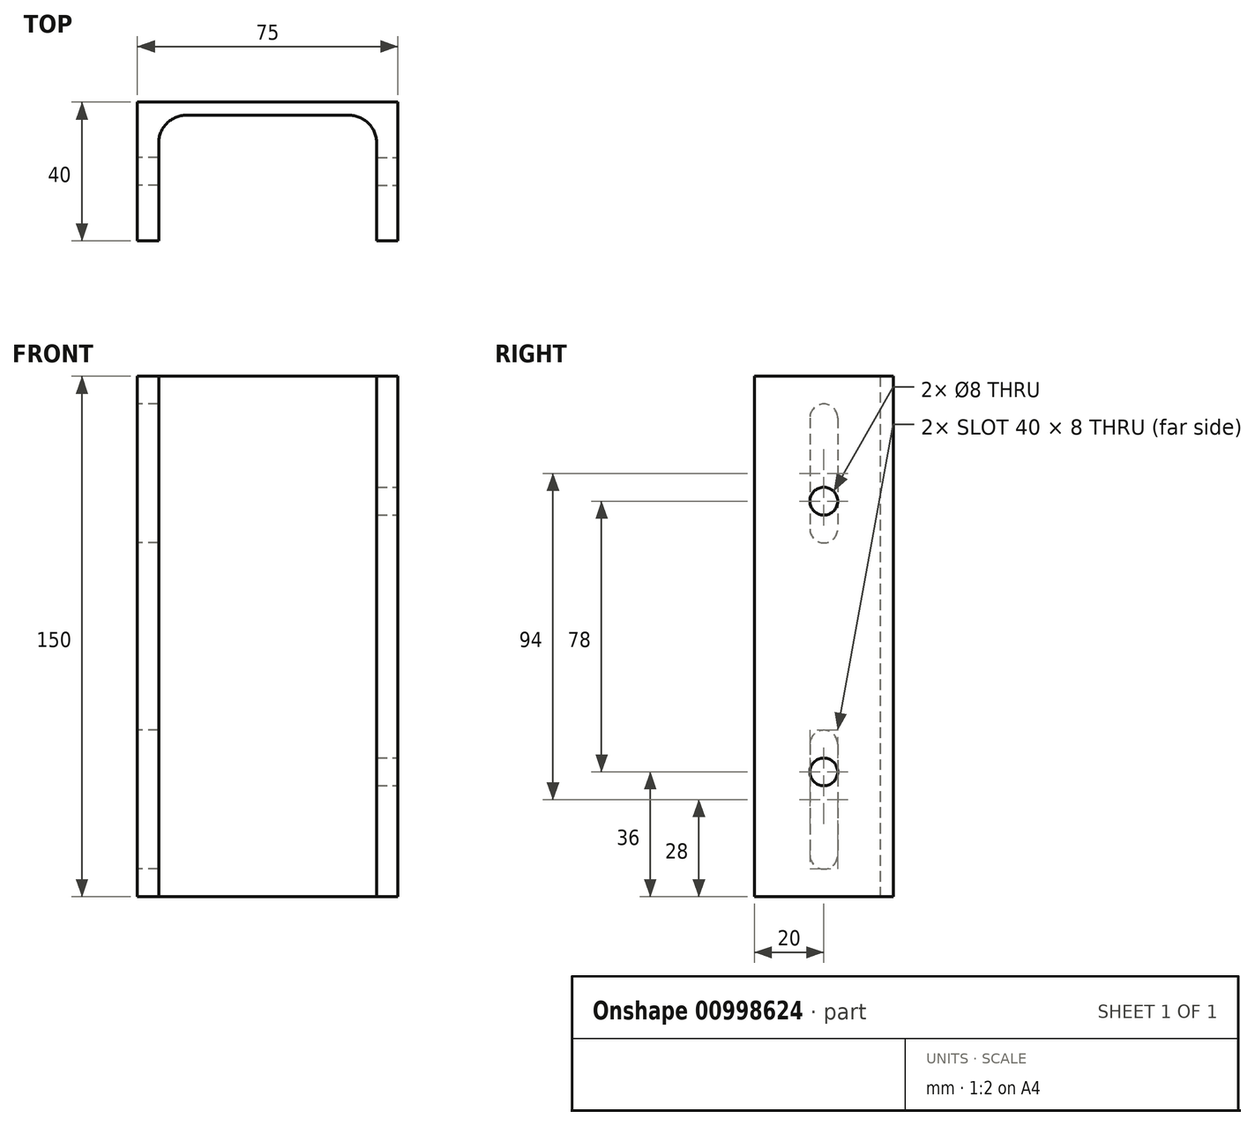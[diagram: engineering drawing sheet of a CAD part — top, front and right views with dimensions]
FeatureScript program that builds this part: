
annotation { "Feature Type Name" : "Feature", "Feature Type Description" : "" }
export const myFeature = defineFeature(function(context is Context, id is Id, definition is map)
    precondition{}
    {
        {
            var Q0;
            Q0=qCreatedBy(makeId("Top.planeOp"),FACE);
            var sketch = newSketch(context, id + "F0", { "sketchPlane" : qUnion([Q0])});
            skLineSegment(sketch, "E0", {"start": v(-37.5, 0) * mm, "end": v(37.5, 0) * mm});
            skLineSegment(sketch, "E1", {"start": v(-37.5, 0) * mm, "end": v(-37.5, -40) * mm});
            skLineSegment(sketch, "E2", {"start": v(37.5, 0) * mm, "end": v(37.5, -40) * mm});
            skLineSegment(sketch, "E3", {"start": v(-31.4, -11.8) * mm, "end": v(-31.4, -40) * mm});
            skLineSegment(sketch, "E4", {"start": v(-31.4, -40) * mm, "end": v(-37.5, -40) * mm});
            skLineSegment(sketch, "E5", {"start": v(31.4, -11.8) * mm, "end": v(31.4, -40) * mm});
            skLineSegment(sketch, "E6", {"start": v(31.4, -40) * mm, "end": v(37.5, -40) * mm});
            skArc(sketch, "E7", {"start": v(-23.4, -3.8) * mm, "mid": v(-29.06, -6.14) * mm, "end": v(-31.4, -11.8) * mm});
            skArc(sketch, "E8", {"start": v(31.4, -11.8) * mm, "mid": v(29.06, -6.14) * mm, "end": v(23.4, -3.8) * mm});
            skLineSegment(sketch, "E9.trimOffspring", {"start": v(-23.4, -3.8) * mm, "end": v(23.4, -3.8) * mm});
            skSolve(sketch);
        }
        {
            var Q0;
            Q0=makeQuery(id+"F0.imprint","IMPRINT",FACE,{"disambiguationData":[TD([[makeQuery(id+"F0.imprint","IMPRINT",EDGE,{"derivedFrom":sQuery(id+"F0.wireOp",EDGE,"E0")}),-1.0]])]});
            extrude(context, id + "F1", {"entities" : qUnion([Q0]), "depth" : 150 * mm, "offsetDistance" : 25 * mm});
        }
        {
            var Q0;
            Q0=makeQuery(id+"F1.opExtrude","SWEPT_FACE",FACE,{"disambiguationData":[OSD([sQuery(id+"F0.wireOp",EDGE,"E2")])]});
            var sketch = newSketch(context, id + "F2", { "sketchPlane" : qUnion([Q0])});
            skPoint(sketch, "E10", {"position": v(-20, 36) * mm});
            skPoint(sketch, "E11", {"position": v(-20, 114) * mm});
            skSolve(sketch);
        }
        {
            var Q0;
            Q0=sQuery(id+"F2.wireOp",VERTEX,"E11");
            var Q1;
            Q1=sQuery(id+"F2.wireOp",VERTEX,"E10");
            var Q2;
            Q2=makeQuery(id+"F1.opExtrude","SWEPT_BODY",BODY,{"disambiguationData":[OSD([sQuery(id+"F0.wireOp",EDGE,"E0"),sQuery(id+"F0.wireOp",EDGE,"E1"),sQuery(id+"F0.wireOp",EDGE,"E2"),sQuery(id+"F0.wireOp",EDGE,"E3"),sQuery(id+"F0.wireOp",EDGE,"E4"),sQuery(id+"F0.wireOp",EDGE,"E5"),sQuery(id+"F0.wireOp",EDGE,"E6"),sQuery(id+"F0.wireOp",EDGE,"E7"),sQuery(id+"F0.wireOp",EDGE,"E8"),sQuery(id+"F0.wireOp",EDGE,"E9.trimOffspring")])]});
            hole(context, id + "F3", {"style" : HoleStyle.SIMPLE, "endStyle" : HoleEndStyle.BLIND, "holeDiameter" : 8 * mm, "majorDiameter" : 5 * mm, "holeDepth" : 7 * mm, "tappedDepth" : 12 * mm, "tapClearance" : 3, "locations" : qUnion([Q0, Q1]), "scope" : qUnion([Q2])});
        }
        {
            var Q0;
            Q0=makeQuery(id+"F1.opExtrude","SWEPT_FACE",FACE,{"disambiguationData":[OSD([sQuery(id+"F0.wireOp",EDGE,"E1")])]});
            var sketch = newSketch(context, id + "F4", { "sketchPlane" : qUnion([Q0])});
            skCircle(sketch, "E12", {"center": v(20, 12) * mm, "radius": 4 * mm});
            skPoint(sketch, "E12.centerSnap0", {"position": v(20, 0) * mm});
            skCircle(sketch, "E13", {"center": v(20, 44) * mm, "radius": 4 * mm});
            skPoint(sketch, "E13.centerSnap0", {"position": v(20, 150) * mm});
            skLineSegment(sketch, "E14", {"start": v(16, 44.18) * mm, "end": v(16, 11.82) * mm});
            skLineSegment(sketch, "E15", {"start": v(24, 44) * mm, "end": v(24, 12) * mm});
            skArc(sketch, "E16", {"start": v(24, 138) * mm, "mid": v(20, 142) * mm, "end": v(16, 138) * mm});
            skCircle(sketch, "E17", {"center": v(20, 106) * mm, "radius": 4 * mm});
            skLineSegment(sketch, "E18", {"start": v(16, 138) * mm, "end": v(16, 106) * mm});
            skLineSegment(sketch, "E19", {"start": v(24, 138) * mm, "end": v(24, 106) * mm});
            skSolve(sketch);
        }
        {
            var Q0;
            Q0=makeQuery(id+"F4.imprint","IMPRINT",FACE,{"disambiguationData":[TD([[makeQuery(id+"F4.imprint","IMPRINT",EDGE,{"derivedFrom":sQuery(id+"F4.wireOp",EDGE,"E16")}),1.0]])]});
            var Q1;
            {var subQ0=sQuery(id+"F4.wireOp",EDGE,"E17");var subQ1=makeQuery(id+"F4.imprint","INTERSECT",VERTEX,{"derivedFrom":[subQ0,sQuery(id+"F4.wireOp",EDGE,"E18")]});Q1=makeQuery(id+"F4.imprint","IMPRINT",FACE,{"disambiguationData":[TD([[makeQuery(id+"F4.imprint","IMPRINT",EDGE,{"disambiguationData":[TD([[subQ1,1.0]])],"derivedFrom":subQ0}),1.0]])]});}
            var Q2;
            {var subQ0=sQuery(id+"F4.wireOp",EDGE,"E14");var subQ1=sQuery(id+"F4.wireOp",EDGE,"E13");var subQ2=makeQuery(id+"F4.imprint","INTERSECT",VERTEX,{"disambiguationData":[OD(0.0)],"derivedFrom":[subQ1,subQ0]});Q2=makeQuery(id+"F4.imprint","IMPRINT",FACE,{"disambiguationData":[TD([[makeQuery(id+"F4.imprint","IMPRINT",EDGE,{"disambiguationData":[TD([[subQ2,1.0]])],"derivedFrom":subQ1}),1.0]])]});}
            var Q3;
            {var subQ0=sQuery(id+"F4.wireOp",EDGE,"E12");var subQ1=makeQuery(id+"F4.imprint","INTERSECT",VERTEX,{"derivedFrom":[subQ0,sQuery(id+"F4.wireOp",EDGE,"E15")]});Q3=makeQuery(id+"F4.imprint","IMPRINT",FACE,{"disambiguationData":[TD([[makeQuery(id+"F4.imprint","IMPRINT",EDGE,{"disambiguationData":[TD([[subQ1,-1.0]])],"derivedFrom":subQ0}),1.0]])]});}
            var Q4;
            {var subQ0=sQuery(id+"F4.wireOp",EDGE,"E15");Q4=makeQuery(id+"F4.imprint","IMPRINT",FACE,{"disambiguationData":[TD([[makeQuery(id+"F4.imprint","IMPRINT",EDGE,{"derivedFrom":subQ0}),-1.0]])]});}
            var Q5;
            Q5=makeQuery(id+"F1.opExtrude","SWEPT_FACE",FACE,{"disambiguationData":[OSD([sQuery(id+"F0.wireOp",EDGE,"E3")])]});
            extrude(context, id + "F5", {"entities" : qUnion([Q0, Q1, Q2, Q3, Q4]), "operationType" : NewBodyOperationType.REMOVE, "endBound" : BoundingType.UP_TO_SURFACE, "oppositeDirection" : true, "depth" : 25 * mm, "endBoundEntityFace" : qUnion([Q5]), "offsetDistance" : 25 * mm});
        }
    });
